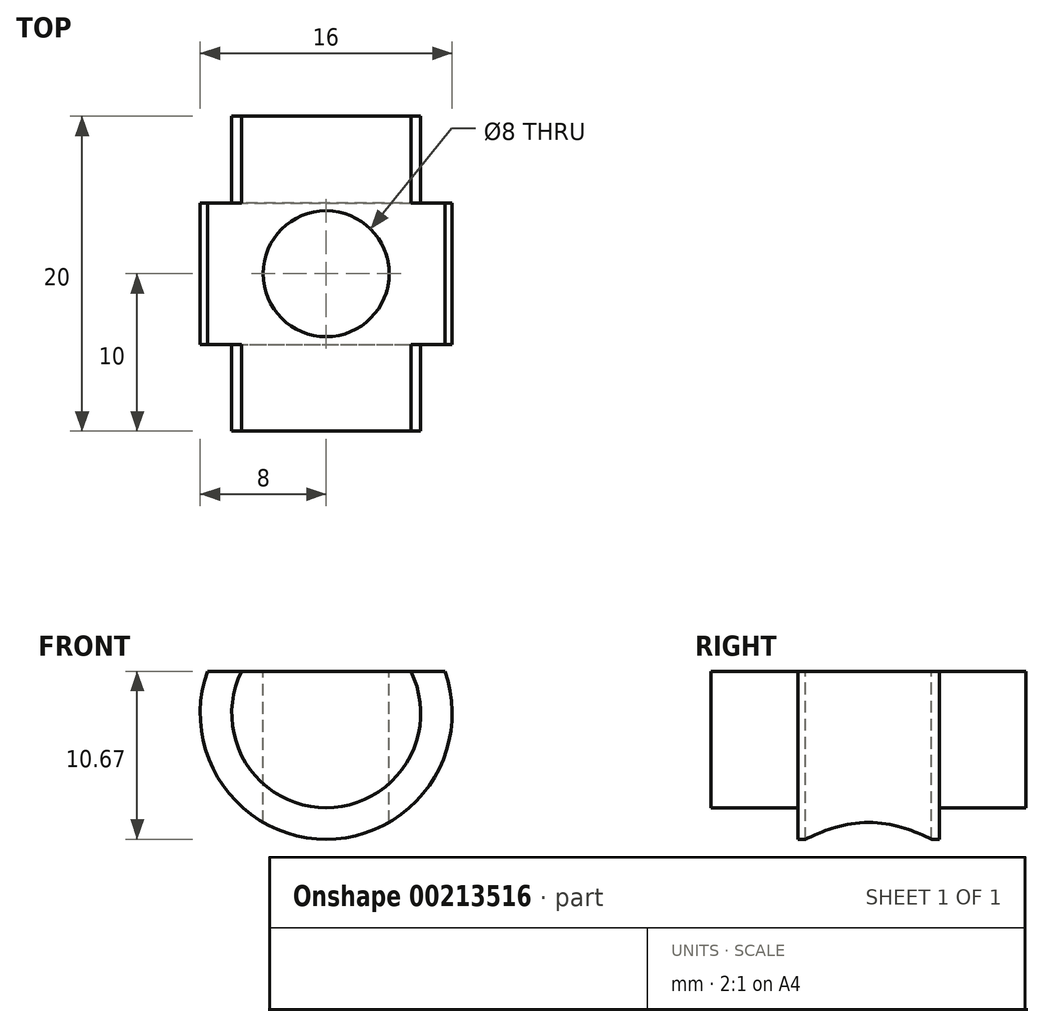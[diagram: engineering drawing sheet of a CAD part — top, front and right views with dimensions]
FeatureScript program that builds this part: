
annotation { "Feature Type Name" : "Feature", "Feature Type Description" : "" }
export const myFeature = defineFeature(function(context is Context, id is Id, definition is map)
    precondition{}
    {
        {
            var Q0;
            Q0=qCreatedBy(makeId("Front.planeOp"),FACE);
            var sketch = newSketch(context, id + "F0", { "sketchPlane" : qUnion([Q0])});
            skLineSegment(sketch, "E0", {"start": v(-8, 0) * mm, "end": v(-8, 0) * mm});
            skArc(sketch, "E1", {"start": v(-8, 0) * mm, "mid": v(1.35, -7.88) * mm, "end": v(7.54, 2.67) * mm});
            skLineSegment(sketch, "E2", {"start": v(7.54, 2.67) * mm, "end": v(-7.54, 2.67) * mm});
            skArc(sketch, "E3.trimOffspring", {"start": v(-7.54, 2.67) * mm, "mid": v(-7.88, 1.35) * mm, "end": v(-8, 0) * mm});
            skSolve(sketch);
        }
        {
            var Q0;
            Q0 = qSketchRegion(id + "F0", true);
            extrude(context, id + "F1", {"entities" : qUnion([Q0]), "depth" : 9 * mm});
        }
        {
            var Q0;
            Q0=makeQuery(id+"F1.opExtrude","SWEPT_FACE",FACE,{"disambiguationData":[OSD([sQuery(id+"F0.wireOp",EDGE,"E2")])]});
            var sketch = newSketch(context, id + "F2", { "sketchPlane" : qUnion([Q0])});
            skPoint(sketch, "E4", {"position": v(0, -4.5) * mm});
            skPoint(sketch, "E4.positionSnap0", {"position": v(-7.54, -4.5) * mm});
            skSolve(sketch);
        }
        {
            var Q0;
            Q0=sQuery(id+"F2.wireOp",VERTEX,"E4");
            var Q1;
            Q1=makeQuery(id+"F1.opExtrude","SWEPT_BODY",BODY,{"disambiguationData":[OSD([sQuery(id+"F0.wireOp",EDGE,"E0"),sQuery(id+"F0.wireOp",EDGE,"E1"),sQuery(id+"F0.wireOp",EDGE,"E2"),sQuery(id+"F0.wireOp",EDGE,"E3.trimOffspring")])]});
            hole(context, id + "F3", {"style" : HoleStyle.SIMPLE, "endStyle" : HoleEndStyle.THROUGH, "holeDiameter" : 8 * mm, "locations" : qUnion([Q0]), "scope" : qUnion([Q1]), "isTappedThrough" : true});
        }
        {
            var Q0;
            Q0=makeQuery(id+"F1.opExtrude","CAP_FACE",FACE,{"disambiguationData":[OSD([sQuery(id+"F0.wireOp",EDGE,"E1"),sQuery(id+"F0.wireOp",EDGE,"E2"),sQuery(id+"F0.wireOp",EDGE,"E3.trimOffspring")])],"isStart":false});
            var sketch = newSketch(context, id + "F4", { "sketchPlane" : qUnion([Q0])});
            skArc(sketch, "E5", {"start": v(-5.37, 2.67) * mm, "mid": v(0, -6) * mm, "end": v(5.37, 2.67) * mm});
            skLineSegment(sketch, "E6", {"start": v(-5.37, 2.67) * mm, "end": v(5.37, 2.67) * mm});
            skSolve(sketch);
        }
        {
            var Q0;
            Q0 = qSketchRegion(id + "F4", true);
            extrude(context, id + "F5", {"entities" : qUnion([Q0]), "operationType" : NewBodyOperationType.ADD, "depth" : 5.5 * mm});
        }
        {
            var Q0;
            Q0=makeQuery(id+"F1.opExtrude","CAP_FACE",FACE,{"disambiguationData":[OSD([sQuery(id+"F0.wireOp",EDGE,"E1"),sQuery(id+"F0.wireOp",EDGE,"E2"),sQuery(id+"F0.wireOp",EDGE,"E3.trimOffspring")])],"isStart":true});
            var sketch = newSketch(context, id + "F6", { "sketchPlane" : qUnion([Q0])});
            skArc(sketch, "E7", {"start": v(-5.37, 2.67) * mm, "mid": v(0, -6) * mm, "end": v(5.37, 2.67) * mm});
            skLineSegment(sketch, "E8", {"start": v(5.37, 2.67) * mm, "end": v(-5.37, 2.67) * mm});
            skSolve(sketch);
        }
        {
            var Q0;
            Q0 = qSketchRegion(id + "F6", true);
            extrude(context, id + "F7", {"entities" : qUnion([Q0]), "operationType" : NewBodyOperationType.ADD, "depth" : 5.5 * mm});
        }
    });
